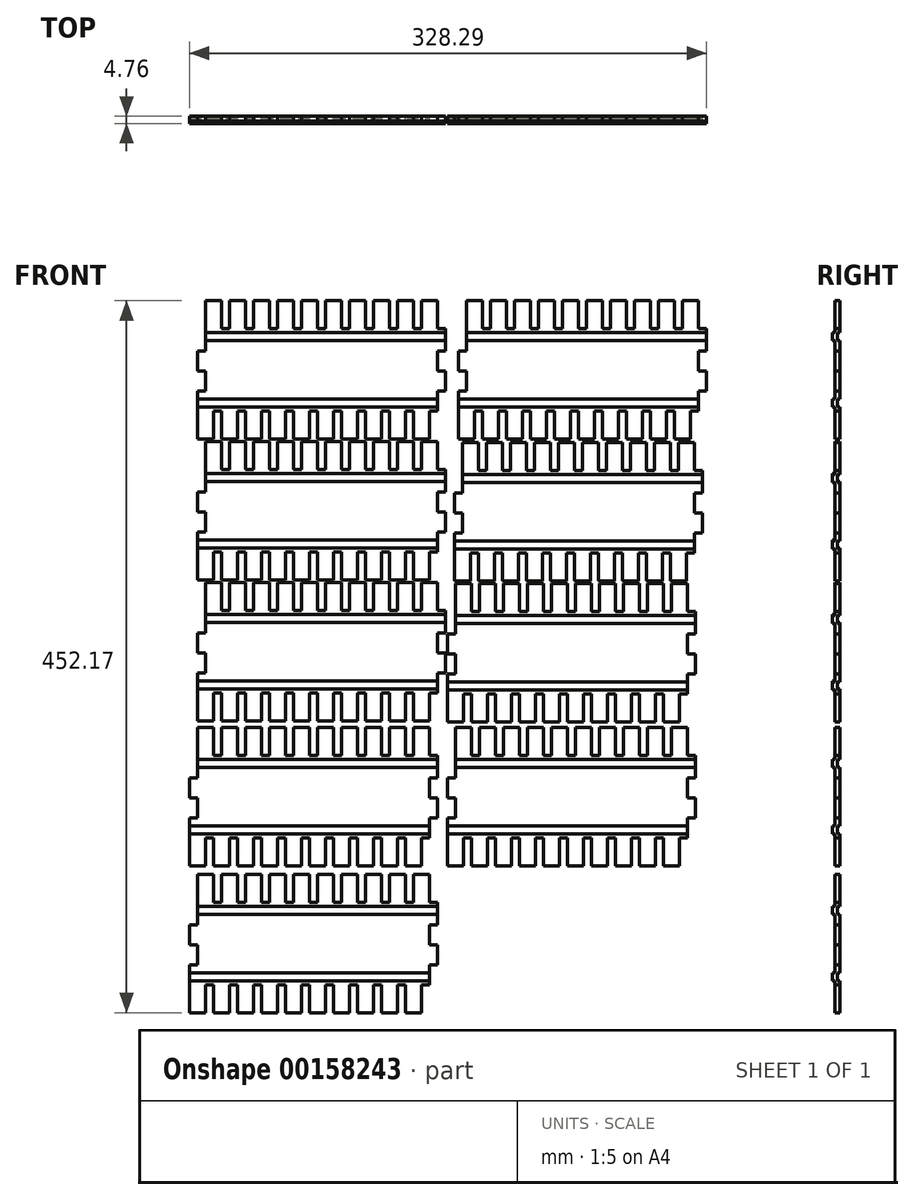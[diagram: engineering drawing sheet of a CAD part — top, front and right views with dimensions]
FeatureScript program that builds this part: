
annotation { "Feature Type Name" : "Feature", "Feature Type Description" : "" }
export const myFeature = defineFeature(function(context is Context, id is Id, definition is map)
    precondition{}
    {
        {
            var Q0;
            Q0=qCreatedBy(makeId("Front.planeOp"),FACE);
            var sketch = newSketch(context, id + "F0", { "sketchPlane" : qUnion([Q0])});
            skLineSegment(sketch, "E0", {"start": v(-40.64, -21.9) * mm, "end": v(111.76, -21.9) * mm});
            skLineSegment(sketch, "E1", {"start": v(-40.64, -21.9) * mm, "end": v(-40.64, -26.98) * mm});
            skLineSegment(sketch, "E2", {"start": v(-40.64, -26.98) * mm, "end": v(111.76, -26.98) * mm});
            skLineSegment(sketch, "E3", {"start": v(111.76, -26.98) * mm, "end": v(111.76, -21.9) * mm});
            skLineSegment(sketch, "E4", {"start": v(-35.56, 20.06) * mm, "end": v(116.84, 20.06) * mm});
            skLineSegment(sketch, "E5", {"start": v(116.84, 20.06) * mm, "end": v(116.84, 14.98) * mm});
            skLineSegment(sketch, "E6", {"start": v(116.84, 14.98) * mm, "end": v(-35.56, 14.98) * mm});
            skLineSegment(sketch, "E7", {"start": v(-35.56, 14.98) * mm, "end": v(-35.56, 20.06) * mm});
            skLineSegment(sketch, "E8", {"start": v(-40.64, -21.9) * mm, "end": v(-40.64, -16.82) * mm});
            skLineSegment(sketch, "E9", {"start": v(-40.64, -16.82) * mm, "end": v(-35.57, -16.82) * mm});
            skLineSegment(sketch, "E10", {"start": v(-35.57, -16.82) * mm, "end": v(-35.57, -4.12) * mm});
            skLineSegment(sketch, "E11", {"start": v(-35.57, -4.12) * mm, "end": v(-40.64, -4.12) * mm});
            skLineSegment(sketch, "E12", {"start": v(-40.64, -4.12) * mm, "end": v(-40.64, 8.58) * mm});
            skLineSegment(sketch, "E13", {"start": v(-40.64, 8.58) * mm, "end": v(-35.56, 8.58) * mm});
            skLineSegment(sketch, "E14", {"start": v(-35.56, 8.58) * mm, "end": v(-35.56, 14.98) * mm});
            skLineSegment(sketch, "E15", {"start": v(116.84, 14.98) * mm, "end": v(116.84, 8.58) * mm});
            skLineSegment(sketch, "E16", {"start": v(116.84, 8.58) * mm, "end": v(111.76, 8.58) * mm});
            skLineSegment(sketch, "E17", {"start": v(111.76, 8.58) * mm, "end": v(111.76, -4.12) * mm});
            skLineSegment(sketch, "E18", {"start": v(111.76, -4.12) * mm, "end": v(116.84, -4.12) * mm});
            skLineSegment(sketch, "E19", {"start": v(116.84, -4.12) * mm, "end": v(116.84, -16.82) * mm});
            skLineSegment(sketch, "E20", {"start": v(116.84, -16.82) * mm, "end": v(111.76, -16.82) * mm});
            skLineSegment(sketch, "E21", {"start": v(111.76, -16.82) * mm, "end": v(111.76, -21.9) * mm});
            skLineSegment(sketch, "E22", {"start": v(-35.56, 20.06) * mm, "end": v(-35.56, 40.38) * mm});
            skLineSegment(sketch, "E23", {"start": v(-35.56, 40.38) * mm, "end": v(-25.4, 40.38) * mm});
            skLineSegment(sketch, "E24", {"start": v(-25.4, 40.38) * mm, "end": v(-25.4, 22.6) * mm});
            skLineSegment(sketch, "E25", {"start": v(-25.4, 22.6) * mm, "end": v(-20.32, 22.6) * mm});
            skLineSegment(sketch, "E26", {"start": v(-20.32, 22.6) * mm, "end": v(-20.32, 40.38) * mm});
            skLineSegment(sketch, "E27", {"start": v(-20.32, 40.38) * mm, "end": v(-10.16, 40.38) * mm});
            skLineSegment(sketch, "E28", {"start": v(-10.16, 40.38) * mm, "end": v(-10.16, 22.6) * mm});
            skLineSegment(sketch, "E29", {"start": v(-10.16, 22.6) * mm, "end": v(-5.08, 22.6) * mm});
            skLineSegment(sketch, "E30", {"start": v(-5.08, 22.6) * mm, "end": v(-5.08, 40.38) * mm});
            skLineSegment(sketch, "E31", {"start": v(-5.08, 40.38) * mm, "end": v(5.08, 40.38) * mm});
            skLineSegment(sketch, "E32", {"start": v(5.08, 40.38) * mm, "end": v(5.08, 22.6) * mm});
            skLineSegment(sketch, "E33", {"start": v(5.08, 22.6) * mm, "end": v(10.16, 22.6) * mm});
            skLineSegment(sketch, "E34", {"start": v(10.16, 22.6) * mm, "end": v(10.16, 40.38) * mm});
            skLineSegment(sketch, "E35", {"start": v(10.16, 40.38) * mm, "end": v(20.32, 40.38) * mm});
            skLineSegment(sketch, "E36", {"start": v(20.32, 40.38) * mm, "end": v(20.32, 22.6) * mm});
            skLineSegment(sketch, "E37", {"start": v(20.32, 22.6) * mm, "end": v(25.4, 22.6) * mm});
            skLineSegment(sketch, "E38", {"start": v(25.4, 22.6) * mm, "end": v(25.4, 40.38) * mm});
            skLineSegment(sketch, "E39", {"start": v(25.4, 40.38) * mm, "end": v(35.56, 40.38) * mm});
            skLineSegment(sketch, "E40", {"start": v(35.56, 40.38) * mm, "end": v(35.56, 22.6) * mm});
            skLineSegment(sketch, "E41", {"start": v(35.56, 22.6) * mm, "end": v(40.64, 22.6) * mm});
            skLineSegment(sketch, "E42", {"start": v(40.64, 22.6) * mm, "end": v(40.64, 40.38) * mm});
            skLineSegment(sketch, "E43", {"start": v(40.64, 40.38) * mm, "end": v(50.8, 40.38) * mm});
            skLineSegment(sketch, "E44", {"start": v(50.8, 40.38) * mm, "end": v(50.8, 22.6) * mm});
            skLineSegment(sketch, "E45", {"start": v(50.8, 22.6) * mm, "end": v(55.88, 22.6) * mm});
            skLineSegment(sketch, "E46", {"start": v(55.88, 22.6) * mm, "end": v(55.88, 40.38) * mm});
            skLineSegment(sketch, "E47", {"start": v(-40.64, -26.98) * mm, "end": v(-40.64, -47.3) * mm});
            skLineSegment(sketch, "E48", {"start": v(-40.64, -47.3) * mm, "end": v(-30.48, -47.3) * mm});
            skLineSegment(sketch, "E49", {"start": v(-30.48, -47.3) * mm, "end": v(-30.48, -29.52) * mm});
            skLineSegment(sketch, "E50", {"start": v(-30.48, -29.52) * mm, "end": v(-25.4, -29.52) * mm});
            skLineSegment(sketch, "E51", {"start": v(-25.4, -29.52) * mm, "end": v(-25.4, -47.3) * mm});
            skLineSegment(sketch, "E52", {"start": v(-25.4, -47.3) * mm, "end": v(-15.24, -47.3) * mm});
            skLineSegment(sketch, "E53", {"start": v(-15.24, -47.3) * mm, "end": v(-15.24, -29.52) * mm});
            skLineSegment(sketch, "E54", {"start": v(-15.24, -29.52) * mm, "end": v(-10.16, -29.52) * mm});
            skLineSegment(sketch, "E55", {"start": v(-10.16, -29.52) * mm, "end": v(-10.16, -47.3) * mm});
            skLineSegment(sketch, "E56", {"start": v(-10.16, -47.3) * mm, "end": v(0, -47.3) * mm});
            skLineSegment(sketch, "E57", {"start": v(0, -47.3) * mm, "end": v(0, -29.52) * mm});
            skLineSegment(sketch, "E58", {"start": v(0, -29.52) * mm, "end": v(5.08, -29.52) * mm});
            skLineSegment(sketch, "E59", {"start": v(5.08, -29.52) * mm, "end": v(5.08, -47.3) * mm});
            skLineSegment(sketch, "E60", {"start": v(5.08, -47.3) * mm, "end": v(15.24, -47.3) * mm});
            skLineSegment(sketch, "E61", {"start": v(15.24, -47.3) * mm, "end": v(15.24, -29.52) * mm});
            skLineSegment(sketch, "E62", {"start": v(15.24, -29.52) * mm, "end": v(20.32, -29.52) * mm});
            skLineSegment(sketch, "E63", {"start": v(20.32, -29.52) * mm, "end": v(20.32, -47.3) * mm});
            skLineSegment(sketch, "E64", {"start": v(20.32, -47.3) * mm, "end": v(30.48, -47.3) * mm});
            skLineSegment(sketch, "E65", {"start": v(30.48, -47.3) * mm, "end": v(30.48, -29.52) * mm});
            skLineSegment(sketch, "E66", {"start": v(30.48, -29.52) * mm, "end": v(35.56, -29.52) * mm});
            skLineSegment(sketch, "E67", {"start": v(35.56, -29.52) * mm, "end": v(35.56, -47.3) * mm});
            skLineSegment(sketch, "E68", {"start": v(35.56, -47.3) * mm, "end": v(45.72, -47.3) * mm});
            skLineSegment(sketch, "E69", {"start": v(45.72, -47.3) * mm, "end": v(45.72, -29.52) * mm});
            skLineSegment(sketch, "E70", {"start": v(45.72, -29.52) * mm, "end": v(50.8, -29.52) * mm});
            skLineSegment(sketch, "E71", {"start": v(50.8, -29.52) * mm, "end": v(50.8, -47.3) * mm});
            skLineSegment(sketch, "E72", {"start": v(55.88, 40.38) * mm, "end": v(66.04, 40.38) * mm});
            skLineSegment(sketch, "E73", {"start": v(66.04, 40.38) * mm, "end": v(66.04, 22.6) * mm});
            skLineSegment(sketch, "E74", {"start": v(66.04, 22.6) * mm, "end": v(71.12, 22.6) * mm});
            skLineSegment(sketch, "E75", {"start": v(71.12, 22.6) * mm, "end": v(71.12, 40.38) * mm});
            skLineSegment(sketch, "E76", {"start": v(71.12, 40.38) * mm, "end": v(81.28, 40.38) * mm});
            skLineSegment(sketch, "E77", {"start": v(81.28, 40.38) * mm, "end": v(81.28, 22.6) * mm});
            skLineSegment(sketch, "E78", {"start": v(81.28, 22.6) * mm, "end": v(86.36, 22.6) * mm});
            skLineSegment(sketch, "E79", {"start": v(86.36, 22.6) * mm, "end": v(86.36, 40.38) * mm});
            skLineSegment(sketch, "E80", {"start": v(86.36, 40.38) * mm, "end": v(96.52, 40.38) * mm});
            skLineSegment(sketch, "E81", {"start": v(96.52, 40.38) * mm, "end": v(96.52, 22.6) * mm});
            skLineSegment(sketch, "E82", {"start": v(96.52, 22.6) * mm, "end": v(101.6, 22.6) * mm});
            skLineSegment(sketch, "E83", {"start": v(101.6, 22.6) * mm, "end": v(101.6, 40.38) * mm});
            skLineSegment(sketch, "E84", {"start": v(101.6, 40.38) * mm, "end": v(111.76, 40.38) * mm});
            skLineSegment(sketch, "E85", {"start": v(111.76, 40.38) * mm, "end": v(111.76, 22.6) * mm});
            skLineSegment(sketch, "E86", {"start": v(111.76, 22.6) * mm, "end": v(116.84, 22.6) * mm});
            skLineSegment(sketch, "E87", {"start": v(50.8, -47.3) * mm, "end": v(60.96, -47.3) * mm});
            skLineSegment(sketch, "E88", {"start": v(60.96, -47.3) * mm, "end": v(60.96, -29.52) * mm});
            skLineSegment(sketch, "E89", {"start": v(60.96, -29.52) * mm, "end": v(66.04, -29.52) * mm});
            skLineSegment(sketch, "E90", {"start": v(66.04, -29.52) * mm, "end": v(66.04, -47.3) * mm});
            skLineSegment(sketch, "E91", {"start": v(66.04, -47.3) * mm, "end": v(76.2, -47.3) * mm});
            skLineSegment(sketch, "E92", {"start": v(76.2, -47.3) * mm, "end": v(76.2, -29.52) * mm});
            skLineSegment(sketch, "E93", {"start": v(76.2, -29.52) * mm, "end": v(81.28, -29.52) * mm});
            skLineSegment(sketch, "E94", {"start": v(81.28, -29.52) * mm, "end": v(81.28, -47.3) * mm});
            skLineSegment(sketch, "E95", {"start": v(81.28, -47.3) * mm, "end": v(91.44, -47.3) * mm});
            skLineSegment(sketch, "E96", {"start": v(91.44, -47.3) * mm, "end": v(91.44, -29.52) * mm});
            skLineSegment(sketch, "E97", {"start": v(91.44, -29.52) * mm, "end": v(96.52, -29.52) * mm});
            skLineSegment(sketch, "E98", {"start": v(96.52, -29.52) * mm, "end": v(96.52, -47.3) * mm});
            skLineSegment(sketch, "E99", {"start": v(96.52, -47.3) * mm, "end": v(106.68, -47.3) * mm});
            skLineSegment(sketch, "E100", {"start": v(106.68, -47.3) * mm, "end": v(106.68, -29.52) * mm});
            skLineSegment(sketch, "E101", {"start": v(106.68, -29.52) * mm, "end": v(111.76, -29.52) * mm});
            skLineSegment(sketch, "E102", {"start": v(116.84, 22.6) * mm, "end": v(116.84, 20.06) * mm});
            skLineSegment(sketch, "E103", {"start": v(111.76, -29.52) * mm, "end": v(111.76, -26.98) * mm});
            skSolve(sketch);
        }
        {
            var Q0;
            Q0=makeQuery(id+"F0.imprint","IMPRINT",FACE,{"disambiguationData":[TD([[makeQuery(id+"F0.imprint","IMPRINT",EDGE,{"derivedFrom":sQuery(id+"F0.wireOp",EDGE,"E2")}),-1.0]])]});
            var Q1;
            Q1=makeQuery(id+"F0.imprint","IMPRINT",FACE,{"disambiguationData":[TD([[makeQuery(id+"F0.imprint","IMPRINT",EDGE,{"derivedFrom":sQuery(id+"F0.wireOp",EDGE,"E0")}),1.0]])]});
            var Q2;
            Q2=makeQuery(id+"F0.imprint","IMPRINT",FACE,{"disambiguationData":[TD([[makeQuery(id+"F0.imprint","IMPRINT",EDGE,{"derivedFrom":sQuery(id+"F0.wireOp",EDGE,"E0")}),1.0]])]});
            var Q3;
            Q3=makeQuery(id+"F0.imprint","IMPRINT",FACE,{"disambiguationData":[TD([[makeQuery(id+"F0.imprint","IMPRINT",EDGE,{"derivedFrom":sQuery(id+"F0.wireOp",EDGE,"E4")}),1.0]])]});
            extrude(context, id + "F1", {"entities" : qUnion([Q0, Q1, Q2, Q3]), "endBound" : BoundingType.SYMMETRIC, "depth" : 3.17 * mm});
        }
        {
            var Q0;
            Q0=makeQuery(id+"F0.imprint","IMPRINT",FACE,{"disambiguationData":[TD([[makeQuery(id+"F0.imprint","IMPRINT",EDGE,{"derivedFrom":sQuery(id+"F0.wireOp",EDGE,"E4")}),-1.0]])]});
            var Q1;
            Q1=makeQuery(id+"F0.imprint","IMPRINT",FACE,{"disambiguationData":[TD([[makeQuery(id+"F0.imprint","IMPRINT",EDGE,{"derivedFrom":sQuery(id+"F0.wireOp",EDGE,"E0")}),-1.0]])]});
            extrude(context, id + "F2", {"entities" : qUnion([Q0, Q1]), "operationType" : NewBodyOperationType.ADD, "depth" : 3.17 * mm});
        }
        {
            var Q0;
            Q0=makeQuery(id+"F1.opExtrude","SWEPT_BODY",BODY,{"disambiguationData":[OSD([sQuery(id+"F0.wireOp",EDGE,"E0"),sQuery(id+"F0.wireOp",EDGE,"E6"),sQuery(id+"F0.wireOp",EDGE,"E8"),sQuery(id+"F0.wireOp",EDGE,"E9"),sQuery(id+"F0.wireOp",EDGE,"E10"),sQuery(id+"F0.wireOp",EDGE,"E11"),sQuery(id+"F0.wireOp",EDGE,"E12"),sQuery(id+"F0.wireOp",EDGE,"E13"),sQuery(id+"F0.wireOp",EDGE,"E14"),sQuery(id+"F0.wireOp",EDGE,"E15"),sQuery(id+"F0.wireOp",EDGE,"E16"),sQuery(id+"F0.wireOp",EDGE,"E17"),sQuery(id+"F0.wireOp",EDGE,"E18"),sQuery(id+"F0.wireOp",EDGE,"E19"),sQuery(id+"F0.wireOp",EDGE,"E20"),sQuery(id+"F0.wireOp",EDGE,"E21")])]});
            transform(context, id + "F3", {"entities" : qUnion([Q0]), "transformType" : TransformType.TRANSLATION_3D, "dx" : 2.54 * mm, "dy" : 0 * mm, "dz" : 90.17 * mm, "makeCopy" : true});
        }
        {
            var Q0;
            Q0=makeQuery(id+"F1.opExtrude","SWEPT_BODY",BODY,{"disambiguationData":[OSD([sQuery(id+"F0.wireOp",EDGE,"E0"),sQuery(id+"F0.wireOp",EDGE,"E6"),sQuery(id+"F0.wireOp",EDGE,"E8"),sQuery(id+"F0.wireOp",EDGE,"E9"),sQuery(id+"F0.wireOp",EDGE,"E10"),sQuery(id+"F0.wireOp",EDGE,"E11"),sQuery(id+"F0.wireOp",EDGE,"E12"),sQuery(id+"F0.wireOp",EDGE,"E13"),sQuery(id+"F0.wireOp",EDGE,"E14"),sQuery(id+"F0.wireOp",EDGE,"E15"),sQuery(id+"F0.wireOp",EDGE,"E16"),sQuery(id+"F0.wireOp",EDGE,"E17"),sQuery(id+"F0.wireOp",EDGE,"E18"),sQuery(id+"F0.wireOp",EDGE,"E19"),sQuery(id+"F0.wireOp",EDGE,"E20"),sQuery(id+"F0.wireOp",EDGE,"E21")])]});
            transform(context, id + "F4", {"entities" : qUnion([Q0]), "transformType" : TransformType.TRANSLATION_3D, "dx" : -4.44 * mm, "dy" : 0 * mm, "dz" : -89.53 * mm, "makeCopy" : true});
        }
        {
            var Q0;
            Q0=makeQuery(id+"F4.opPattern","COPY",BODY,{"derivedFrom":makeQuery(id+"F1.opExtrude","SWEPT_BODY",BODY,{"disambiguationData":[OSD([sQuery(id+"F0.wireOp",EDGE,"E0"),sQuery(id+"F0.wireOp",EDGE,"E6"),sQuery(id+"F0.wireOp",EDGE,"E8"),sQuery(id+"F0.wireOp",EDGE,"E9"),sQuery(id+"F0.wireOp",EDGE,"E10"),sQuery(id+"F0.wireOp",EDGE,"E11"),sQuery(id+"F0.wireOp",EDGE,"E12"),sQuery(id+"F0.wireOp",EDGE,"E13"),sQuery(id+"F0.wireOp",EDGE,"E14"),sQuery(id+"F0.wireOp",EDGE,"E15"),sQuery(id+"F0.wireOp",EDGE,"E16"),sQuery(id+"F0.wireOp",EDGE,"E17"),sQuery(id+"F0.wireOp",EDGE,"E18"),sQuery(id+"F0.wireOp",EDGE,"E19"),sQuery(id+"F0.wireOp",EDGE,"E20"),sQuery(id+"F0.wireOp",EDGE,"E21")])]}),"instanceName":"1"});
            transform(context, id + "F5", {"entities" : qUnion([Q0]), "transformType" : TransformType.TRANSLATION_3D, "dx" : -158.75 * mm, "dy" : 0 * mm, "dz" : 0.63 * mm, "makeCopy" : true});
        }
        {
            var Q0;
            Q0=makeQuery(id+"F5.opPattern","COPY",BODY,{"derivedFrom":makeQuery(id+"F4.opPattern","COPY",BODY,{"derivedFrom":makeQuery(id+"F1.opExtrude","SWEPT_BODY",BODY,{"disambiguationData":[OSD([sQuery(id+"F0.wireOp",EDGE,"E0"),sQuery(id+"F0.wireOp",EDGE,"E6"),sQuery(id+"F0.wireOp",EDGE,"E8"),sQuery(id+"F0.wireOp",EDGE,"E9"),sQuery(id+"F0.wireOp",EDGE,"E10"),sQuery(id+"F0.wireOp",EDGE,"E11"),sQuery(id+"F0.wireOp",EDGE,"E12"),sQuery(id+"F0.wireOp",EDGE,"E13"),sQuery(id+"F0.wireOp",EDGE,"E14"),sQuery(id+"F0.wireOp",EDGE,"E15"),sQuery(id+"F0.wireOp",EDGE,"E16"),sQuery(id+"F0.wireOp",EDGE,"E17"),sQuery(id+"F0.wireOp",EDGE,"E18"),sQuery(id+"F0.wireOp",EDGE,"E19"),sQuery(id+"F0.wireOp",EDGE,"E20"),sQuery(id+"F0.wireOp",EDGE,"E21")])]}),"instanceName":"1"}),"instanceName":"1"});
            transform(context, id + "F6", {"entities" : qUnion([Q0]), "transformType" : TransformType.TRANSLATION_3D, "dx" : 0 * mm, "dy" : 0 * mm, "dz" : 89.53 * mm, "makeCopy" : true});
        }
        {
            var Q0;
            Q0=makeQuery(id+"F6.opPattern","COPY",BODY,{"derivedFrom":makeQuery(id+"F5.opPattern","COPY",BODY,{"derivedFrom":makeQuery(id+"F4.opPattern","COPY",BODY,{"derivedFrom":makeQuery(id+"F1.opExtrude","SWEPT_BODY",BODY,{"disambiguationData":[OSD([sQuery(id+"F0.wireOp",EDGE,"E0"),sQuery(id+"F0.wireOp",EDGE,"E6"),sQuery(id+"F0.wireOp",EDGE,"E8"),sQuery(id+"F0.wireOp",EDGE,"E9"),sQuery(id+"F0.wireOp",EDGE,"E10"),sQuery(id+"F0.wireOp",EDGE,"E11"),sQuery(id+"F0.wireOp",EDGE,"E12"),sQuery(id+"F0.wireOp",EDGE,"E13"),sQuery(id+"F0.wireOp",EDGE,"E14"),sQuery(id+"F0.wireOp",EDGE,"E15"),sQuery(id+"F0.wireOp",EDGE,"E16"),sQuery(id+"F0.wireOp",EDGE,"E17"),sQuery(id+"F0.wireOp",EDGE,"E18"),sQuery(id+"F0.wireOp",EDGE,"E19"),sQuery(id+"F0.wireOp",EDGE,"E20"),sQuery(id+"F0.wireOp",EDGE,"E21")])]}),"instanceName":"1"}),"instanceName":"1"}),"instanceName":"1"});
            transform(context, id + "F7", {"entities" : qUnion([Q0]), "transformType" : TransformType.TRANSLATION_3D, "dx" : 0 * mm, "dy" : 0 * mm, "dz" : 89.53 * mm, "makeCopy" : true});
        }
        {
            var Q0;
            Q0=makeQuery(id+"F4.opPattern","COPY",BODY,{"derivedFrom":makeQuery(id+"F1.opExtrude","SWEPT_BODY",BODY,{"disambiguationData":[OSD([sQuery(id+"F0.wireOp",EDGE,"E0"),sQuery(id+"F0.wireOp",EDGE,"E6"),sQuery(id+"F0.wireOp",EDGE,"E8"),sQuery(id+"F0.wireOp",EDGE,"E9"),sQuery(id+"F0.wireOp",EDGE,"E10"),sQuery(id+"F0.wireOp",EDGE,"E11"),sQuery(id+"F0.wireOp",EDGE,"E12"),sQuery(id+"F0.wireOp",EDGE,"E13"),sQuery(id+"F0.wireOp",EDGE,"E14"),sQuery(id+"F0.wireOp",EDGE,"E15"),sQuery(id+"F0.wireOp",EDGE,"E16"),sQuery(id+"F0.wireOp",EDGE,"E17"),sQuery(id+"F0.wireOp",EDGE,"E18"),sQuery(id+"F0.wireOp",EDGE,"E19"),sQuery(id+"F0.wireOp",EDGE,"E20"),sQuery(id+"F0.wireOp",EDGE,"E21")])]}),"instanceName":"1"});
            transform(context, id + "F8", {"entities" : qUnion([Q0]), "transformType" : TransformType.TRANSLATION_3D, "dx" : 0 * mm, "dy" : 0 * mm, "dz" : -91.44 * mm, "makeCopy" : true});
        }
        {
            var Q0;
            Q0=makeQuery(id+"F8.opPattern","COPY",BODY,{"derivedFrom":makeQuery(id+"F4.opPattern","COPY",BODY,{"derivedFrom":makeQuery(id+"F1.opExtrude","SWEPT_BODY",BODY,{"disambiguationData":[OSD([sQuery(id+"F0.wireOp",EDGE,"E0"),sQuery(id+"F0.wireOp",EDGE,"E6"),sQuery(id+"F0.wireOp",EDGE,"E8"),sQuery(id+"F0.wireOp",EDGE,"E9"),sQuery(id+"F0.wireOp",EDGE,"E10"),sQuery(id+"F0.wireOp",EDGE,"E11"),sQuery(id+"F0.wireOp",EDGE,"E12"),sQuery(id+"F0.wireOp",EDGE,"E13"),sQuery(id+"F0.wireOp",EDGE,"E14"),sQuery(id+"F0.wireOp",EDGE,"E15"),sQuery(id+"F0.wireOp",EDGE,"E16"),sQuery(id+"F0.wireOp",EDGE,"E17"),sQuery(id+"F0.wireOp",EDGE,"E18"),sQuery(id+"F0.wireOp",EDGE,"E19"),sQuery(id+"F0.wireOp",EDGE,"E20"),sQuery(id+"F0.wireOp",EDGE,"E21")])]}),"instanceName":"1"}),"instanceName":"1"});
            transform(context, id + "F9", {"entities" : qUnion([Q0]), "transformType" : TransformType.TRANSLATION_3D, "dx" : -163.83 * mm, "dy" : 0 * mm, "dz" : 0 * mm, "makeCopy" : true});
        }
        {
            var Q0;
            Q0=makeQuery(id+"F9.opPattern","COPY",BODY,{"derivedFrom":makeQuery(id+"F8.opPattern","COPY",BODY,{"derivedFrom":makeQuery(id+"F4.opPattern","COPY",BODY,{"derivedFrom":makeQuery(id+"F1.opExtrude","SWEPT_BODY",BODY,{"disambiguationData":[OSD([sQuery(id+"F0.wireOp",EDGE,"E0"),sQuery(id+"F0.wireOp",EDGE,"E6"),sQuery(id+"F0.wireOp",EDGE,"E8"),sQuery(id+"F0.wireOp",EDGE,"E9"),sQuery(id+"F0.wireOp",EDGE,"E10"),sQuery(id+"F0.wireOp",EDGE,"E11"),sQuery(id+"F0.wireOp",EDGE,"E12"),sQuery(id+"F0.wireOp",EDGE,"E13"),sQuery(id+"F0.wireOp",EDGE,"E14"),sQuery(id+"F0.wireOp",EDGE,"E15"),sQuery(id+"F0.wireOp",EDGE,"E16"),sQuery(id+"F0.wireOp",EDGE,"E17"),sQuery(id+"F0.wireOp",EDGE,"E18"),sQuery(id+"F0.wireOp",EDGE,"E19"),sQuery(id+"F0.wireOp",EDGE,"E20"),sQuery(id+"F0.wireOp",EDGE,"E21")])]}),"instanceName":"1"}),"instanceName":"1"}),"instanceName":"1"});
            transform(context, id + "F10", {"entities" : qUnion([Q0]), "transformType" : TransformType.TRANSLATION_3D, "dx" : 0 * mm, "dy" : 0 * mm, "dz" : -93.34 * mm, "makeCopy" : true});
        }
    });
